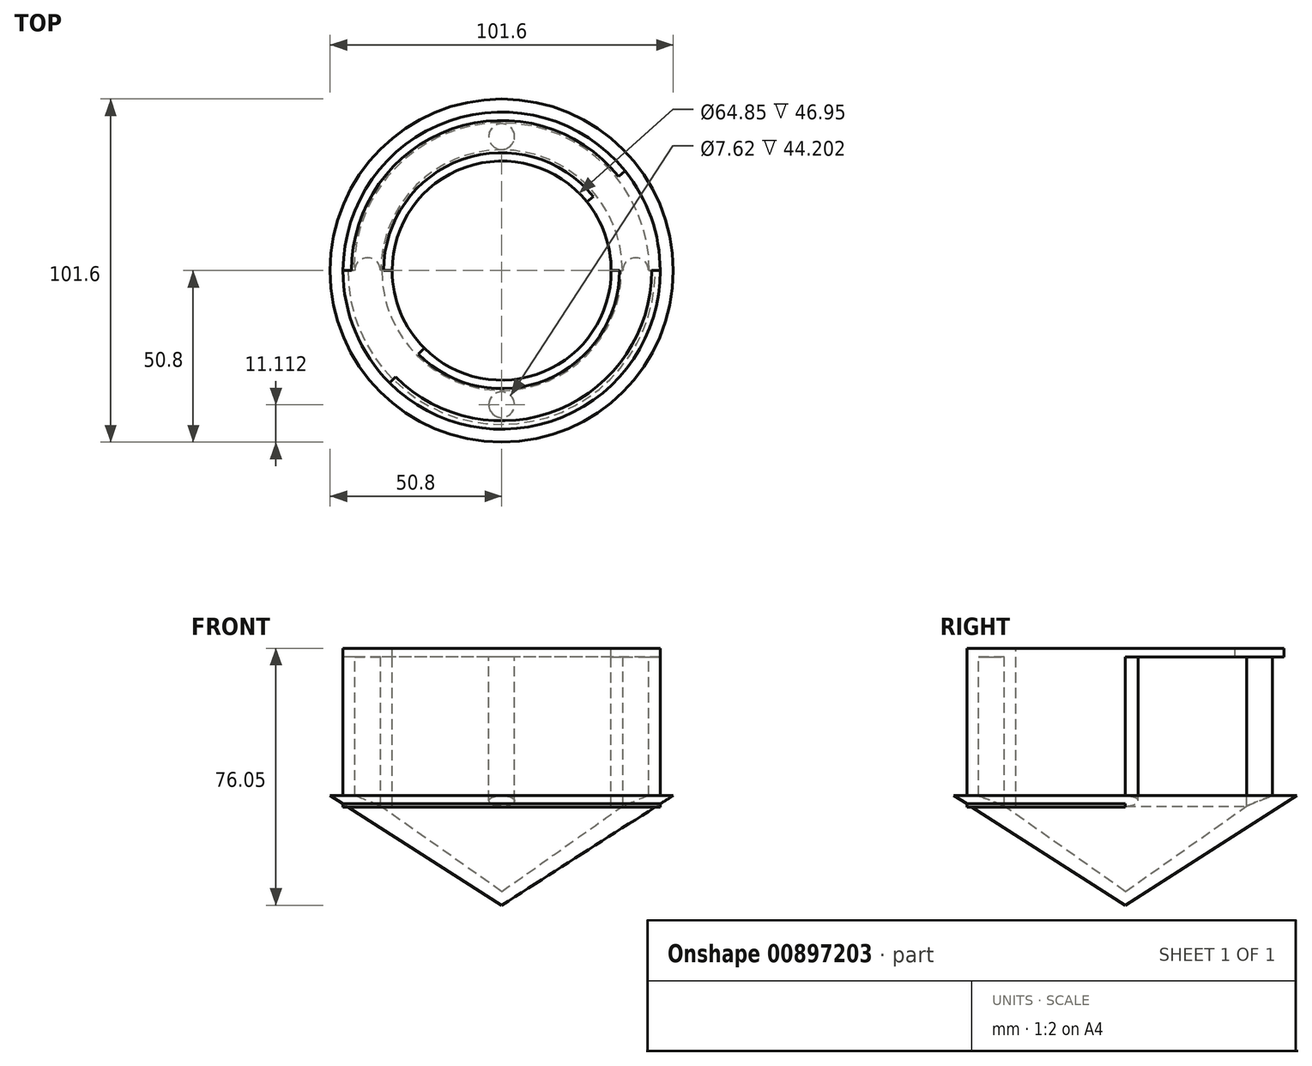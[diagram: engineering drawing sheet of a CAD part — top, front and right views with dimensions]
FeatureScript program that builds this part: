
annotation { "Feature Type Name" : "Feature", "Feature Type Description" : "" }
export const myFeature = defineFeature(function(context is Context, id is Id, definition is map)
    precondition{}
    {
        {
            var Q0;
            Q0=qCreatedBy(makeId("Top.planeOp"),FACE);
            var sketch = newSketch(context, id + "F0", { "sketchPlane" : qUnion([Q0])});
            skCircle(sketch, "E0", {"center": v(0, 0) * mm, "radius": 34.93 * mm});
            skCircle(sketch, "E1", {"center": v(0, 0) * mm, "radius": 44.45 * mm});
            skCircle(sketch, "E2", {"center": v(0, 0) * mm, "radius": 32.43 * mm});
            skCircle(sketch, "E3", {"center": v(0, 0) * mm, "radius": 46.95 * mm});
            skLineSegment(sketch, "E4", {"start": v(0, 0) * mm, "end": v(46.95, 0) * mm});
            skLineSegment(sketch, "E5", {"start": v(23.47, -23.48) * mm, "end": v(0, 0) * mm});
            skLineSegment(sketch, "E6", {"start": v(0, 0) * mm, "end": v(33.2, -33.2) * mm});
            skLineSegment(sketch, "E7", {"start": v(36.55, 29.47) * mm, "end": v(0, 0) * mm});
            skLineSegment(sketch, "E8", {"start": v(0, 0) * mm, "end": v(-33.2, 33.2) * mm});
            skLineSegment(sketch, "E9", {"start": v(-33.2, 33.2) * mm, "end": v(0, 0) * mm});
            skLineSegment(sketch, "E10", {"start": v(0, 0) * mm, "end": v(-33.2, -33.2) * mm});
            skLineSegment(sketch, "E11", {"start": v(-46.95, 0) * mm, "end": v(46.95, 0) * mm});
            skSolve(sketch);
        }
        {
            var Q0;
            {var subQ0=sQuery(id+"F0.wireOp",EDGE,"E10");var subQ1=sQuery(id+"F0.wireOp",EDGE,"E1");var subQ2=makeQuery(id+"F0.imprint","INTERSECT",VERTEX,{"derivedFrom":[subQ1,subQ0]});Q0=makeQuery(id+"F0.imprint","IMPRINT",FACE,{"disambiguationData":[TD([[makeQuery(id+"F0.imprint","IMPRINT",EDGE,{"disambiguationData":[TD([[subQ2,-1.0]])],"derivedFrom":subQ1}),-1.0]])]});}
            var Q1;
            {var subQ0=sQuery(id+"F0.wireOp",EDGE,"E7");var subQ1=sQuery(id+"F0.wireOp",EDGE,"E1");var subQ2=makeQuery(id+"F0.imprint","INTERSECT",VERTEX,{"derivedFrom":[subQ1,subQ0]});Q1=makeQuery(id+"F0.imprint","IMPRINT",FACE,{"disambiguationData":[TD([[makeQuery(id+"F0.imprint","IMPRINT",EDGE,{"disambiguationData":[TD([[subQ2,-1.0]])],"derivedFrom":subQ1}),-1.0]])]});}
            var Q2;
            {var subQ0=sQuery(id+"F0.wireOp",EDGE,"E11");var subQ1=sQuery(id+"F0.wireOp",EDGE,"E1");var subQ2=makeQuery(id+"F0.imprint","INTERSECT",VERTEX,{"derivedFrom":[subQ1,subQ0]});Q2=makeQuery(id+"F0.imprint","IMPRINT",FACE,{"disambiguationData":[TD([[makeQuery(id+"F0.imprint","IMPRINT",EDGE,{"disambiguationData":[TD([[subQ2,1.0]])],"derivedFrom":subQ1}),-1.0]])]});}
            var Q3;
            {var subQ0=sQuery(id+"F0.wireOp",EDGE,"E4");var subQ1=sQuery(id+"F0.wireOp",EDGE,"E1");var subQ2=makeQuery(id+"F0.imprint","INTERSECT",VERTEX,{"derivedFrom":[subQ1,subQ0]});Q3=makeQuery(id+"F0.imprint","IMPRINT",FACE,{"disambiguationData":[TD([[makeQuery(id+"F0.imprint","IMPRINT",EDGE,{"disambiguationData":[TD([[subQ2,1.0]])],"derivedFrom":subQ1}),-1.0]])]});}
            var Q4;
            {var subQ0=sQuery(id+"F0.wireOp",EDGE,"E6");var subQ1=sQuery(id+"F0.wireOp",EDGE,"E0");var subQ2=makeQuery(id+"F0.imprint","INTERSECT",VERTEX,{"derivedFrom":[subQ1,subQ0]});Q4=makeQuery(id+"F0.imprint","IMPRINT",FACE,{"disambiguationData":[TD([[makeQuery(id+"F0.imprint","IMPRINT",EDGE,{"disambiguationData":[TD([[subQ2,1.0]])],"derivedFrom":subQ1}),1.0]])]});}
            var Q5;
            {var subQ3=sQuery(id+"F0.wireOp",EDGE,"E6");var subQ6=sQuery(id+"F0.wireOp",EDGE,"E0");var subQ9=makeQuery(id+"F0.imprint","INTERSECT",VERTEX,{"derivedFrom":[subQ6,subQ3]});Q5=makeQuery(id+"F0.imprint","IMPRINT",FACE,{"disambiguationData":[TD([[makeQuery(id+"F0.imprint","IMPRINT",EDGE,{"disambiguationData":[TD([[subQ9,-1.0]])],"derivedFrom":subQ6}),1.0]])]});}
            var Q6;
            {var subQ0=sQuery(id+"F0.wireOp",EDGE,"E7");var subQ1=sQuery(id+"F0.wireOp",EDGE,"E0");var subQ2=makeQuery(id+"F0.imprint","INTERSECT",VERTEX,{"derivedFrom":[subQ1,subQ0]});Q6=makeQuery(id+"F0.imprint","IMPRINT",FACE,{"disambiguationData":[TD([[makeQuery(id+"F0.imprint","IMPRINT",EDGE,{"disambiguationData":[TD([[subQ2,-1.0]])],"derivedFrom":subQ1}),1.0]])]});}
            var Q7;
            {var subQ0=sQuery(id+"F0.wireOp",EDGE,"E8");var subQ1=sQuery(id+"F0.wireOp",EDGE,"E0");var subQ2=makeQuery(id+"F0.imprint","INTERSECT",VERTEX,{"derivedFrom":[subQ1,subQ0]});Q7=makeQuery(id+"F0.imprint","IMPRINT",FACE,{"disambiguationData":[TD([[makeQuery(id+"F0.imprint","IMPRINT",EDGE,{"disambiguationData":[TD([[subQ2,-1.0]])],"derivedFrom":subQ1}),1.0]])]});}
            extrude(context, id + "F1", {"entities" : qUnion([Q0, Q1, Q2, Q3, Q4, Q5, Q6, Q7]), "depth" : 1 / 50.8 * mm, "offsetDistance" : 25.4 * mm});
        }
        {
            var Q0;
            {var subQ0=sQuery(id+"F0.wireOp",EDGE,"E11");var subQ1=sQuery(id+"F0.wireOp",EDGE,"E1");var subQ2=makeQuery(id+"F0.imprint","INTERSECT",VERTEX,{"derivedFrom":[subQ1,subQ0]});Q0=makeQuery(id+"F0.imprint","IMPRINT",FACE,{"disambiguationData":[TD([[makeQuery(id+"F0.imprint","IMPRINT",EDGE,{"disambiguationData":[TD([[subQ2,-1.0]])],"derivedFrom":subQ1}),-1.0]])]});}
            var Q1;
            {var subQ0=sQuery(id+"F0.wireOp",EDGE,"E10");var subQ1=sQuery(id+"F0.wireOp",EDGE,"E1");var subQ2=makeQuery(id+"F0.imprint","INTERSECT",VERTEX,{"derivedFrom":[subQ1,subQ0]});Q1=makeQuery(id+"F0.imprint","IMPRINT",FACE,{"disambiguationData":[TD([[makeQuery(id+"F0.imprint","IMPRINT",EDGE,{"disambiguationData":[TD([[subQ2,-1.0]])],"derivedFrom":subQ1}),-1.0]])]});}
            var Q2;
            {var subQ0=sQuery(id+"F0.wireOp",EDGE,"E10");var subQ1=sQuery(id+"F0.wireOp",EDGE,"E0");var subQ2=makeQuery(id+"F0.imprint","INTERSECT",VERTEX,{"derivedFrom":[subQ1,subQ0]});Q2=makeQuery(id+"F0.imprint","IMPRINT",FACE,{"disambiguationData":[TD([[makeQuery(id+"F0.imprint","IMPRINT",EDGE,{"disambiguationData":[TD([[subQ2,1.0]])],"derivedFrom":subQ1}),-1.0]])]});}
            var Q3;
            {var subQ0=sQuery(id+"F0.wireOp",EDGE,"E6");var subQ1=sQuery(id+"F0.wireOp",EDGE,"E0");var subQ2=makeQuery(id+"F0.imprint","INTERSECT",VERTEX,{"derivedFrom":[subQ1,subQ0]});Q3=makeQuery(id+"F0.imprint","IMPRINT",FACE,{"disambiguationData":[TD([[makeQuery(id+"F0.imprint","IMPRINT",EDGE,{"disambiguationData":[TD([[subQ2,1.0]])],"derivedFrom":subQ1}),-1.0]])]});}
            var Q4;
            {var subQ0=sQuery(id+"F0.wireOp",EDGE,"E6");var subQ1=sQuery(id+"F0.wireOp",EDGE,"E0");var subQ2=makeQuery(id+"F0.imprint","INTERSECT",VERTEX,{"derivedFrom":[subQ1,subQ0]});Q4=makeQuery(id+"F0.imprint","IMPRINT",FACE,{"disambiguationData":[TD([[makeQuery(id+"F0.imprint","IMPRINT",EDGE,{"disambiguationData":[TD([[subQ2,-1.0]])],"derivedFrom":subQ1}),-1.0]])]});}
            var Q5;
            {var subQ0=sQuery(id+"F0.wireOp",EDGE,"E6");var subQ1=sQuery(id+"F0.wireOp",EDGE,"E0");var subQ2=makeQuery(id+"F0.imprint","INTERSECT",VERTEX,{"derivedFrom":[subQ1,subQ0]});Q5=makeQuery(id+"F0.imprint","IMPRINT",FACE,{"disambiguationData":[TD([[makeQuery(id+"F0.imprint","IMPRINT",EDGE,{"disambiguationData":[TD([[subQ2,1.0]])],"derivedFrom":subQ1}),1.0]])]});}
            var Q6;
            {var subQ0=sQuery(id+"F0.wireOp",EDGE,"E10");var subQ1=sQuery(id+"F0.wireOp",EDGE,"E0");var subQ2=makeQuery(id+"F0.imprint","INTERSECT",VERTEX,{"derivedFrom":[subQ1,subQ0]});Q6=makeQuery(id+"F0.imprint","IMPRINT",FACE,{"disambiguationData":[TD([[makeQuery(id+"F0.imprint","IMPRINT",EDGE,{"disambiguationData":[TD([[subQ2,1.0]])],"derivedFrom":subQ1}),1.0]])]});}
            var Q7;
            {var subQ3=sQuery(id+"F0.wireOp",EDGE,"E6");var subQ6=sQuery(id+"F0.wireOp",EDGE,"E0");var subQ9=makeQuery(id+"F0.imprint","INTERSECT",VERTEX,{"derivedFrom":[subQ6,subQ3]});Q7=makeQuery(id+"F0.imprint","IMPRINT",FACE,{"disambiguationData":[TD([[makeQuery(id+"F0.imprint","IMPRINT",EDGE,{"disambiguationData":[TD([[subQ9,-1.0]])],"derivedFrom":subQ6}),1.0]])]});}
            var Q8;
            {var subQ0=sQuery(id+"F0.wireOp",EDGE,"E4");var subQ1=sQuery(id+"F0.wireOp",EDGE,"E1");var subQ2=makeQuery(id+"F0.imprint","INTERSECT",VERTEX,{"derivedFrom":[subQ1,subQ0]});Q8=makeQuery(id+"F0.imprint","IMPRINT",FACE,{"disambiguationData":[TD([[makeQuery(id+"F0.imprint","IMPRINT",EDGE,{"disambiguationData":[TD([[subQ2,1.0]])],"derivedFrom":subQ1}),-1.0]])]});}
            var Q9;
            {var subQ0=sQuery(id+"F0.wireOp",EDGE,"E7");var subQ1=sQuery(id+"F0.wireOp",EDGE,"E1");var subQ2=makeQuery(id+"F0.imprint","INTERSECT",VERTEX,{"derivedFrom":[subQ1,subQ0]});Q9=makeQuery(id+"F0.imprint","IMPRINT",FACE,{"disambiguationData":[TD([[makeQuery(id+"F0.imprint","IMPRINT",EDGE,{"disambiguationData":[TD([[subQ2,1.0]])],"derivedFrom":subQ1}),-1.0]])]});}
            var Q10;
            {var subQ0=sQuery(id+"F0.wireOp",EDGE,"E7");var subQ1=sQuery(id+"F0.wireOp",EDGE,"E0");var subQ2=makeQuery(id+"F0.imprint","INTERSECT",VERTEX,{"derivedFrom":[subQ1,subQ0]});Q10=makeQuery(id+"F0.imprint","IMPRINT",FACE,{"disambiguationData":[TD([[makeQuery(id+"F0.imprint","IMPRINT",EDGE,{"disambiguationData":[TD([[subQ2,1.0]])],"derivedFrom":subQ1}),-1.0]])]});}
            var Q11;
            {var subQ0=sQuery(id+"F0.wireOp",EDGE,"E7");var subQ1=sQuery(id+"F0.wireOp",EDGE,"E0");var subQ2=makeQuery(id+"F0.imprint","INTERSECT",VERTEX,{"derivedFrom":[subQ1,subQ0]});Q11=makeQuery(id+"F0.imprint","IMPRINT",FACE,{"disambiguationData":[TD([[makeQuery(id+"F0.imprint","IMPRINT",EDGE,{"disambiguationData":[TD([[subQ2,1.0]])],"derivedFrom":subQ1}),1.0]])]});}
            var Q12;
            {var subQ0=sQuery(id+"F0.wireOp",EDGE,"E7");var subQ1=sQuery(id+"F0.wireOp",EDGE,"E0");var subQ2=makeQuery(id+"F0.imprint","INTERSECT",VERTEX,{"derivedFrom":[subQ1,subQ0]});Q12=makeQuery(id+"F0.imprint","IMPRINT",FACE,{"disambiguationData":[TD([[makeQuery(id+"F0.imprint","IMPRINT",EDGE,{"disambiguationData":[TD([[subQ2,-1.0]])],"derivedFrom":subQ1}),-1.0]])]});}
            var Q13;
            {var subQ0=sQuery(id+"F0.wireOp",EDGE,"E8");var subQ1=sQuery(id+"F0.wireOp",EDGE,"E0");var subQ2=makeQuery(id+"F0.imprint","INTERSECT",VERTEX,{"derivedFrom":[subQ1,subQ0]});Q13=makeQuery(id+"F0.imprint","IMPRINT",FACE,{"disambiguationData":[TD([[makeQuery(id+"F0.imprint","IMPRINT",EDGE,{"disambiguationData":[TD([[subQ2,-1.0]])],"derivedFrom":subQ1}),-1.0]])]});}
            var Q14;
            {var subQ0=sQuery(id+"F0.wireOp",EDGE,"E8");var subQ1=sQuery(id+"F0.wireOp",EDGE,"E0");var subQ2=makeQuery(id+"F0.imprint","INTERSECT",VERTEX,{"derivedFrom":[subQ1,subQ0]});Q14=makeQuery(id+"F0.imprint","IMPRINT",FACE,{"disambiguationData":[TD([[makeQuery(id+"F0.imprint","IMPRINT",EDGE,{"disambiguationData":[TD([[subQ2,-1.0]])],"derivedFrom":subQ1}),1.0]])]});}
            var Q15;
            {var subQ0=sQuery(id+"F0.wireOp",EDGE,"E7");var subQ1=sQuery(id+"F0.wireOp",EDGE,"E0");var subQ2=makeQuery(id+"F0.imprint","INTERSECT",VERTEX,{"derivedFrom":[subQ1,subQ0]});Q15=makeQuery(id+"F0.imprint","IMPRINT",FACE,{"disambiguationData":[TD([[makeQuery(id+"F0.imprint","IMPRINT",EDGE,{"disambiguationData":[TD([[subQ2,-1.0]])],"derivedFrom":subQ1}),1.0]])]});}
            var Q16;
            {var subQ0=sQuery(id+"F0.wireOp",EDGE,"E11");var subQ1=sQuery(id+"F0.wireOp",EDGE,"E1");var subQ2=makeQuery(id+"F0.imprint","INTERSECT",VERTEX,{"derivedFrom":[subQ1,subQ0]});Q16=makeQuery(id+"F0.imprint","IMPRINT",FACE,{"disambiguationData":[TD([[makeQuery(id+"F0.imprint","IMPRINT",EDGE,{"disambiguationData":[TD([[subQ2,1.0]])],"derivedFrom":subQ1}),-1.0]])]});}
            var Q17;
            {var subQ0=sQuery(id+"F0.wireOp",EDGE,"E7");var subQ1=sQuery(id+"F0.wireOp",EDGE,"E1");var subQ2=makeQuery(id+"F0.imprint","INTERSECT",VERTEX,{"derivedFrom":[subQ1,subQ0]});Q17=makeQuery(id+"F0.imprint","IMPRINT",FACE,{"disambiguationData":[TD([[makeQuery(id+"F0.imprint","IMPRINT",EDGE,{"disambiguationData":[TD([[subQ2,-1.0]])],"derivedFrom":subQ1}),-1.0]])]});}
            extrude(context, id + "F2", {"entities" : qUnion([Q0, Q1, Q2, Q3, Q4, Q5, Q6, Q7, Q8, Q9, Q10, Q11, Q12, Q13, Q14, Q15, Q16, Q17]), "oppositeDirection" : true, "depth" : 2.5 * mm, "offsetDistance" : 25.4 * mm});
        }
        {
            var Q0;
            Q0=makeQuery(id+"F2.opExtrude","CAP_FACE",FACE,{"disambiguationData":[OSD([sQuery(id+"F0.wireOp",EDGE,"E2"),sQuery(id+"F0.wireOp",EDGE,"E3")])],"isStart":false});
            var sketch = newSketch(context, id + "F3", { "sketchPlane" : qUnion([Q0])});
            skLineSegment(sketch, "E12", {"start": v(0, 46.95) * mm, "end": v(0, 32.43) * mm});
            skLineSegment(sketch, "E13", {"start": v(0, 32.43) * mm, "end": v(0, 39.69) * mm});
            skLineSegment(sketch, "E14", {"start": v(32.43, 0) * mm, "end": v(46.95, 0) * mm});
            skLineSegment(sketch, "E15", {"start": v(0, -32.43) * mm, "end": v(0, -46.95) * mm});
            skLineSegment(sketch, "E16", {"start": v(-32.43, 0) * mm, "end": v(-46.95, 0) * mm});
            skCircle(sketch, "E17", {"center": v(0, 39.69) * mm, "radius": 3.81 * mm});
            skCircle(sketch, "E18", {"center": v(-39.69, 0) * mm, "radius": 3.81 * mm});
            skCircle(sketch, "E19", {"center": v(0, -39.69) * mm, "radius": 3.81 * mm});
            skCircle(sketch, "E20", {"center": v(39.69, 0) * mm, "radius": 3.81 * mm});
            skSolve(sketch);
        }
        {
            var Q0;
            {var subQ0=sQuery(id+"F3.wireOp",EDGE,"E13");var subQ1=sQuery(id+"F3.wireOp",EDGE,"E12");var subQ2=makeQuery(id+"F3.imprint","INTERSECT",VERTEX,{"derivedFrom":[subQ1,subQ0]});Q0=makeQuery(id+"F3.imprint","IMPRINT",FACE,{"disambiguationData":[TD([[makeQuery(id+"F3.imprint","IMPRINT",EDGE,{"disambiguationData":[TD([[subQ2,1.0]])],"derivedFrom":subQ1}),-1.0]])]});}
            var Q1;
            {var subQ0=sQuery(id+"F3.wireOp",EDGE,"E13");var subQ1=sQuery(id+"F3.wireOp",EDGE,"E12");var subQ2=makeQuery(id+"F3.imprint","INTERSECT",VERTEX,{"derivedFrom":[subQ1,subQ0]});Q1=makeQuery(id+"F3.imprint","IMPRINT",FACE,{"disambiguationData":[TD([[makeQuery(id+"F3.imprint","IMPRINT",EDGE,{"disambiguationData":[TD([[subQ2,1.0]])],"derivedFrom":subQ1}),1.0]])]});}
            var Q2;
            {var subQ0=sQuery(id+"F3.wireOp",EDGE,"E20");var subQ1=sQuery(id+"F3.wireOp",EDGE,"E14");var subQ2=makeQuery(id+"F3.imprint","INTERSECT",VERTEX,{"disambiguationData":[OD(0.0)],"derivedFrom":[subQ1,subQ0]});Q2=makeQuery(id+"F3.imprint","IMPRINT",FACE,{"disambiguationData":[TD([[makeQuery(id+"F3.imprint","IMPRINT",EDGE,{"disambiguationData":[TD([[subQ2,-1.0]])],"derivedFrom":subQ1}),1.0]])]});}
            var Q3;
            {var subQ0=sQuery(id+"F3.wireOp",EDGE,"E20");var subQ1=sQuery(id+"F3.wireOp",EDGE,"E14");var subQ2=makeQuery(id+"F3.imprint","INTERSECT",VERTEX,{"disambiguationData":[OD(0.0)],"derivedFrom":[subQ1,subQ0]});Q3=makeQuery(id+"F3.imprint","IMPRINT",FACE,{"disambiguationData":[TD([[makeQuery(id+"F3.imprint","IMPRINT",EDGE,{"disambiguationData":[TD([[subQ2,-1.0]])],"derivedFrom":subQ1}),-1.0]])]});}
            var Q4;
            {var subQ0=sQuery(id+"F3.wireOp",EDGE,"E18");var subQ1=sQuery(id+"F3.wireOp",EDGE,"E16");var subQ2=makeQuery(id+"F3.imprint","INTERSECT",VERTEX,{"disambiguationData":[OD(0.0)],"derivedFrom":[subQ1,subQ0]});Q4=makeQuery(id+"F3.imprint","IMPRINT",FACE,{"disambiguationData":[TD([[makeQuery(id+"F3.imprint","IMPRINT",EDGE,{"disambiguationData":[TD([[subQ2,-1.0]])],"derivedFrom":subQ1}),-1.0]])]});}
            var Q5;
            {var subQ0=sQuery(id+"F3.wireOp",EDGE,"E18");var subQ1=sQuery(id+"F3.wireOp",EDGE,"E16");var subQ2=makeQuery(id+"F3.imprint","INTERSECT",VERTEX,{"disambiguationData":[OD(0.0)],"derivedFrom":[subQ1,subQ0]});Q5=makeQuery(id+"F3.imprint","IMPRINT",FACE,{"disambiguationData":[TD([[makeQuery(id+"F3.imprint","IMPRINT",EDGE,{"disambiguationData":[TD([[subQ2,-1.0]])],"derivedFrom":subQ1}),1.0]])]});}
            var Q6;
            {var subQ0=sQuery(id+"F3.wireOp",EDGE,"E19");var subQ1=sQuery(id+"F3.wireOp",EDGE,"E15");var subQ2=makeQuery(id+"F3.imprint","INTERSECT",VERTEX,{"disambiguationData":[OD(0.0)],"derivedFrom":[subQ1,subQ0]});Q6=makeQuery(id+"F3.imprint","IMPRINT",FACE,{"disambiguationData":[TD([[makeQuery(id+"F3.imprint","IMPRINT",EDGE,{"disambiguationData":[TD([[subQ2,-1.0]])],"derivedFrom":subQ1}),-1.0]])]});}
            var Q7;
            {var subQ0=sQuery(id+"F3.wireOp",EDGE,"E19");var subQ1=sQuery(id+"F3.wireOp",EDGE,"E15");var subQ2=makeQuery(id+"F3.imprint","INTERSECT",VERTEX,{"disambiguationData":[OD(0.0)],"derivedFrom":[subQ1,subQ0]});Q7=makeQuery(id+"F3.imprint","IMPRINT",FACE,{"disambiguationData":[TD([[makeQuery(id+"F3.imprint","IMPRINT",EDGE,{"disambiguationData":[TD([[subQ2,-1.0]])],"derivedFrom":subQ1}),1.0]])]});}
            extrude(context, id + "F4", {"entities" : qUnion([Q0, Q1, Q2, Q3, Q4, Q5, Q6, Q7]), "operationType" : NewBodyOperationType.ADD, "depth" : 44.45 * mm, "offsetDistance" : 25.4 * mm});
        }
        {
            var Q0;
            Q0=qCreatedBy(makeId("Front.planeOp"),FACE);
            var sketch = newSketch(context, id + "F5", { "sketchPlane" : qUnion([Q0])});
            skLineSegment(sketch, "E21", {"start": v(50.8, -43.56) * mm, "end": v(0, -76.03) * mm});
            skLineSegment(sketch, "E22", {"start": v(50.8, -43.56) * mm, "end": v(43.73, -43.56) * mm});
            skLineSegment(sketch, "E23", {"start": v(43.73, -43.56) * mm, "end": v(35.74, -46.75) * mm});
            skLineSegment(sketch, "E24", {"start": v(35.74, -46.75) * mm, "end": v(0, -72.01) * mm});
            skLineSegment(sketch, "E25", {"start": v(0, -76.03) * mm, "end": v(0, -72.01) * mm});
            skSolve(sketch);
        }
        {
            var Q0;
            Q0=makeQuery(id+"F5.imprint","IMPRINT",FACE,{"disambiguationData":[TD([[makeQuery(id+"F5.imprint","IMPRINT",EDGE,{"derivedFrom":sQuery(id+"F5.wireOp",EDGE,"E21")}),-1.0]])]});
            var Q1;
            Q1=sQuery(id+"F5.wireOp",EDGE,"E25");
            revolve(context, id + "F6", {"operationType" : NewBodyOperationType.ADD, "surfaceOperationType" : NewSurfaceOperationType.NEW, "entities" : qUnion([Q0]), "axis" : qUnion([Q1]), "revolveType" : RevolveType.FULL});
        }
    });
